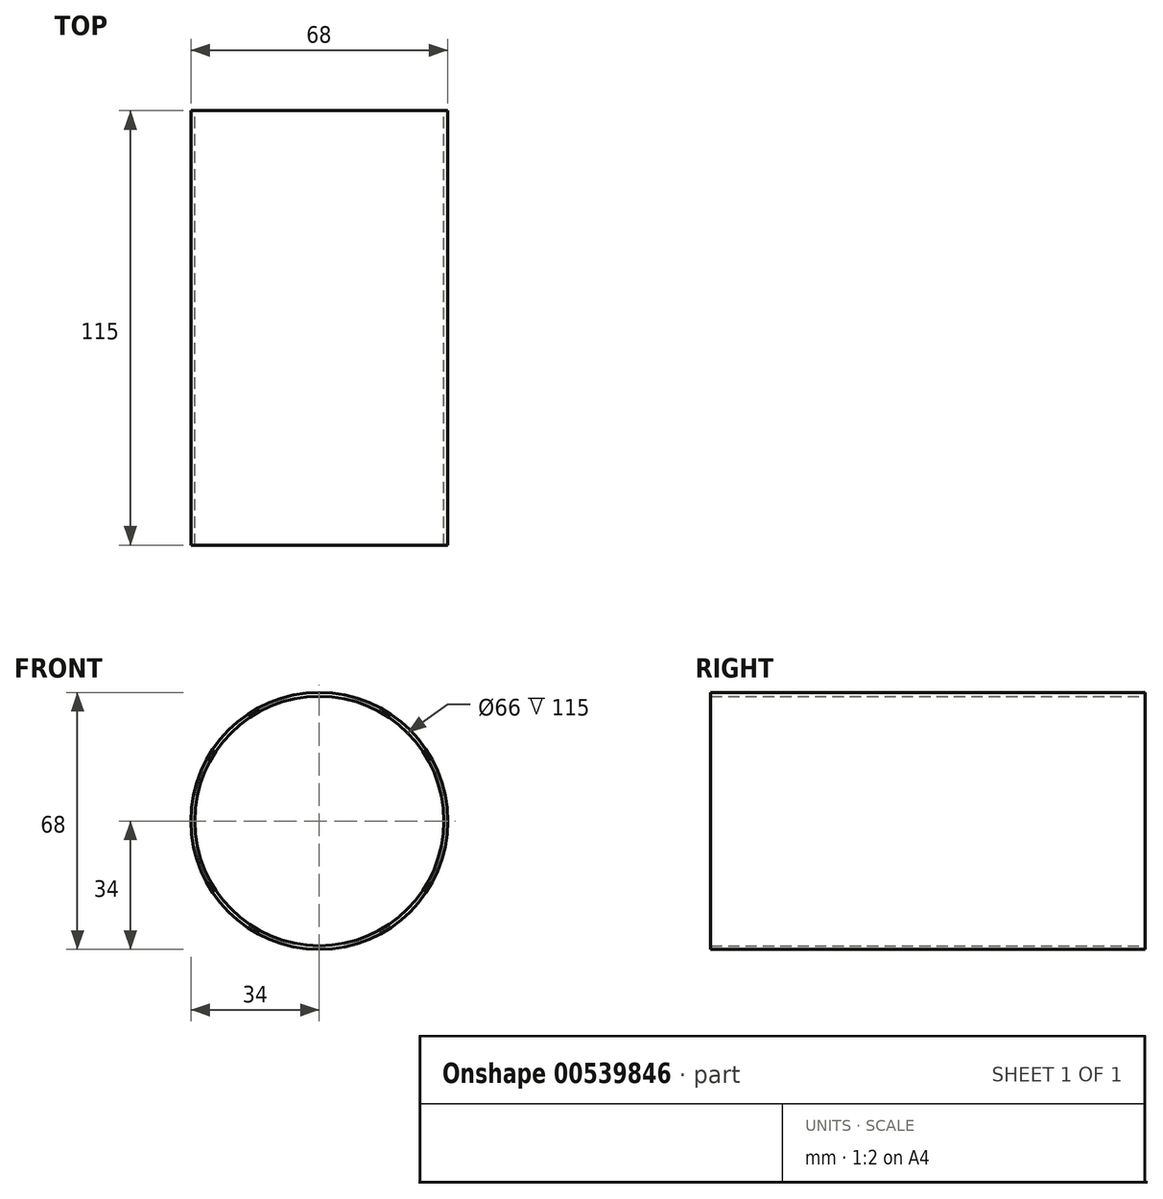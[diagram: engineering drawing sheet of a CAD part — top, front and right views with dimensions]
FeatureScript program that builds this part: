
annotation { "Feature Type Name" : "Feature", "Feature Type Description" : "" }
export const myFeature = defineFeature(function(context is Context, id is Id, definition is map)
    precondition{}
    {
        {
            var Q0;
            Q0=qCreatedBy(makeId("Front.planeOp"),FACE);
            var sketch = newSketch(context, id + "F0", { "sketchPlane" : qUnion([Q0])});
            skCircle(sketch, "E0", {"center": v(0, 0) * mm, "radius": 33 * mm});
            skCircle(sketch, "E1.0", {"center": v(0, 0) * mm, "radius": 34 * mm});
            skSolve(sketch);
        }
        {
            var Q0;
            Q0=makeQuery(id+"F0.imprint","IMPRINT",FACE,{"disambiguationData":[TD([[makeQuery(id+"F0.imprint","IMPRINT",EDGE,{"derivedFrom":sQuery(id+"F0.wireOp",EDGE,"E0")}),-1.0]])]});
            extrude(context, id + "F1", {"entities" : qUnion([Q0]), "depth" : 115 * mm, "offsetDistance" : 25 * mm});
        }
    });
